annotation { "Feature Type Name" : "Feature", "Feature Type Description" : "" }
export const myFeature = defineFeature(function(context is Context, id is Id, definition is map)
    precondition{}
    {
        {
            var Q0;
            Q0=qCreatedBy(makeId("Front.planeOp"),FACE);
            var sketch = newSketch(context, id + "F0", { "sketchPlane" : qUnion([Q0])});
            skLineSegment(sketch, "E0.bottom", {"start": v(-148.5, 105) * mm, "end": v(148.5, 105) * mm});
            skLineSegment(sketch, "E0.top", {"start": v(-148.5, -105) * mm, "end": v(148.5, -105) * mm});
            skLineSegment(sketch, "E0.left", {"start": v(-148.5, 105) * mm, "end": v(-148.5, -105) * mm});
            skLineSegment(sketch, "E0.right", {"start": v(148.5, 105) * mm, "end": v(148.5, -105) * mm});
            skPoint(sketch, "E0.middle", {"position": v(0, 0) * mm});
            skLineSegment(sketch, "E1", {"start": v(-148.5, 75) * mm, "end": v(101.5, 75) * mm});
            skLineSegment(sketch, "E2", {"start": v(101.5, 105) * mm, "end": v(101.5, 75) * mm});
            skLineSegment(sketch, "E3", {"start": v(-148.5, 45) * mm, "end": v(51.5, 45) * mm});
            skLineSegment(sketch, "E4", {"start": v(101.5, 45) * mm, "end": v(101.5, 75) * mm});
            skCircle(sketch, "E5", {"center": v(-133.5, 90) * mm, "radius": 1.5 * mm});
            skCircle(sketch, "E6", {"center": v(-88.5, 90) * mm, "radius": 1.5 * mm});
            skText(sketch, "E7", { "text": "UPPER ARM - INSIDE - LEFT\n    <<< BACK -- FRONT >>>", "fontName": "Arimo-Regular.ttf"});
            skCircle(sketch, "E8.MirrorC", {"center": v(-133.5, 60) * mm, "radius": 1.5 * mm});
            skCircle(sketch, "E9.MirrorC", {"center": v(-88.5, 60) * mm, "radius": 1.5 * mm});
            skText(sketch, "E10", { "text": "UPPER ARM - INSIDE - RIGHT\n   <<< FRONT -- BACK >>>", "fontName": "OpenSans-Regular.ttf"});
            skLineSegment(sketch, "E11.bottom", {"start": v(73, 85) * mm, "end": v(79, 85) * mm});
            skLineSegment(sketch, "E11.top", {"start": v(73, 95) * mm, "end": v(79, 95) * mm});
            skLineSegment(sketch, "E11.left", {"start": v(73, 85) * mm, "end": v(73, 95) * mm});
            skLineSegment(sketch, "E11.right", {"start": v(79, 85) * mm, "end": v(79, 95) * mm});
            skPoint(sketch, "E11.middle", {"position": v(76, 90) * mm});
            skLineSegment(sketch, "E12", {"start": v(-148.5, 15) * mm, "end": v(51.5, 15) * mm});
            skLineSegment(sketch, "E13", {"start": v(51.5, 15) * mm, "end": v(51.5, 45) * mm});
            skLineSegment(sketch, "E14", {"start": v(-148.5, -15) * mm, "end": v(51.5, -15) * mm});
            skLineSegment(sketch, "E15", {"start": v(51.5, -15) * mm, "end": v(51.5, 15) * mm});
            skCircle(sketch, "E16", {"center": v(36.5, 30) * mm, "radius": 1.5 * mm});
            skPoint(sketch, "E16.centerSnap0", {"position": v(51.5, 30) * mm});
            skCircle(sketch, "E17", {"center": v(-53.5, 35) * mm, "radius": 1.5 * mm});
            skCircle(sketch, "E18", {"center": v(-78.5, 25) * mm, "radius": 1.5 * mm});
            skCircle(sketch, "E19", {"center": v(-133.5, 30) * mm, "radius": 1.5 * mm});
            skText(sketch, "E20", { "text": "MIDDLE ARM - INSIDE - LEFT\n   <<< BOTTOM -- TOP >>>", "fontName": "OpenSans-Regular.ttf"});
            skLineSegment(sketch, "E21", {"start": v(-108.5, 45) * mm, "end": v(-108.5, 39) * mm});
            skLineSegment(sketch, "E22", {"start": v(-108.5, 39) * mm, "end": v(-98.5, 39) * mm});
            skLineSegment(sketch, "E23", {"start": v(-98.5, 39) * mm, "end": v(-98.5, 45) * mm});
            skCircle(sketch, "E24.MirrorC", {"center": v(-133.5, 0) * mm, "radius": 1.5 * mm});
            skCircle(sketch, "E25.MirrorC", {"center": v(-53.5, -5) * mm, "radius": 1.5 * mm});
            skCircle(sketch, "E26.MirrorC", {"center": v(-78.5, 5) * mm, "radius": 1.5 * mm});
            skCircle(sketch, "E27.MirrorC", {"center": v(36.5, 0) * mm, "radius": 1.5 * mm});
            skLineSegment(sketch, "E28.MirrorCS", {"start": v(-108.5, -9) * mm, "end": v(-98.5, -9) * mm});
            skLineSegment(sketch, "E29.MirrorCS", {"start": v(-98.5, -9) * mm, "end": v(-98.5, -15) * mm});
            skLineSegment(sketch, "E30.MirrorCS", {"start": v(-108.5, -15) * mm, "end": v(-108.5, -9) * mm});
            skText(sketch, "E31", { "text": "MIDDLE ARM - INSIDE - RIGHT\n   <<< TOP -- BOTTOM >>>", "fontName": "OpenSans-Regular.ttf"});
            skLineSegment(sketch, "E32", {"start": v(51.5, -15) * mm, "end": v(51.5, -85) * mm});
            skLineSegment(sketch, "E33", {"start": v(81.5, 45) * mm, "end": v(118.5, -85.1) * mm});
            skLineSegment(sketch, "E34", {"start": v(51.5, 45) * mm, "end": v(81.5, 45) * mm});
            skLineSegment(sketch, "E35", {"start": v(81.5, 45) * mm, "end": v(101.5, 45) * mm});
            skCircle(sketch, "E36", {"center": v(66.5, 30) * mm, "radius": 1.5 * mm});
            skPoint(sketch, "E36.centerSnap0", {"position": v(66.5, 45) * mm});
            skLineSegment(sketch, "E37", {"start": v(148.5, -85.1) * mm, "end": v(118.5, -85.1) * mm});
            skCircle(sketch, "E38", {"center": v(95.2, -39.74) * mm, "radius": 1.5 * mm});
            skCircle(sketch, "E39", {"center": v(104.8, -0.36) * mm, "radius": 1.5 * mm});
            skCircle(sketch, "E40", {"center": v(133.5, -70.1) * mm, "radius": 1.5 * mm});
            skPoint(sketch, "E40.centerSnap0", {"position": v(133.5, -85.1) * mm});
            skPoint(sketch, "E41.endSnap0", {"position": v(91.5, 45) * mm});
            skLineSegment(sketch, "E42", {"start": v(95.2, -39.74) * mm, "end": v(104.82, -37) * mm, "construction": true});
            skLineSegment(sketch, "E43", {"start": v(104.8, -0.36) * mm, "end": v(95.18, -3.1) * mm, "construction": true});
            skLineSegment(sketch, "E44", {"start": v(51.5, -85) * mm, "end": v(-18.5, -85) * mm});
            skLineSegment(sketch, "E45", {"start": v(-18.5, -85) * mm, "end": v(-18.5, -15) * mm});
            skLineSegment(sketch, "E46", {"start": v(-24.5, -15) * mm, "end": v(-24.5, -25) * mm});
            skLineSegment(sketch, "E47", {"start": v(-24.5, -25) * mm, "end": v(-18.5, -25) * mm});
            skLineSegment(sketch, "E48", {"start": v(-18.5, -35) * mm, "end": v(-24.5, -35) * mm});
            skLineSegment(sketch, "E49", {"start": v(-24.5, -35) * mm, "end": v(-24.5, -45) * mm});
            skLineSegment(sketch, "E50", {"start": v(-24.5, -45) * mm, "end": v(-49.5, -45) * mm});
            skLineSegment(sketch, "E51", {"start": v(-49.5, -45) * mm, "end": v(-49.5, -35) * mm});
            skLineSegment(sketch, "E52", {"start": v(-49.5, -35) * mm, "end": v(-55.5, -35) * mm});
            skLineSegment(sketch, "E53", {"start": v(-55.5, -35) * mm, "end": v(-55.5, -25) * mm});
            skLineSegment(sketch, "E54", {"start": v(-55.5, -25) * mm, "end": v(-49.5, -25) * mm});
            skLineSegment(sketch, "E55", {"start": v(-49.5, -25) * mm, "end": v(-49.5, -15) * mm});
            skLineSegment(sketch, "E56.MirrorCS", {"start": v(-86.5, -15) * mm, "end": v(-86.5, -25) * mm});
            skLineSegment(sketch, "E57.MirrorCS", {"start": v(-61.5, -45) * mm, "end": v(-61.5, -35) * mm});
            skLineSegment(sketch, "E58.MirrorCS", {"start": v(-86.5, -35) * mm, "end": v(-86.5, -45) * mm});
            skLineSegment(sketch, "E59.MirrorCS", {"start": v(-55.5, -25) * mm, "end": v(-61.5, -25) * mm});
            skLineSegment(sketch, "E60.MirrorCS", {"start": v(-86.5, -25) * mm, "end": v(-92.5, -25) * mm});
            skLineSegment(sketch, "E61.MirrorCS", {"start": v(-61.5, -35) * mm, "end": v(-55.5, -35) * mm});
            skLineSegment(sketch, "E62.MirrorCS", {"start": v(-61.5, -25) * mm, "end": v(-61.5, -15) * mm});
            skLineSegment(sketch, "E63.MirrorCS", {"start": v(-86.5, -45) * mm, "end": v(-61.5, -45) * mm});
            skLineSegment(sketch, "E64.MirrorCS", {"start": v(-92.5, -35) * mm, "end": v(-86.5, -35) * mm});
            skLineSegment(sketch, "E65", {"start": v(-92.5, -25) * mm, "end": v(-92.5, -35) * mm});
            skLineSegment(sketch, "E66.MirrorCS", {"start": v(-92.5, -35) * mm, "end": v(-98.5, -35) * mm});
            skLineSegment(sketch, "E67.MirrorCS", {"start": v(-98.5, -25) * mm, "end": v(-92.5, -25) * mm});
            skLineSegment(sketch, "E68.MirrorCS", {"start": v(-98.5, -35) * mm, "end": v(-98.5, -45) * mm});
            skLineSegment(sketch, "E69.MirrorCS", {"start": v(-98.5, -15) * mm, "end": v(-98.5, -25) * mm});
            skLineSegment(sketch, "E70", {"start": v(-98.5, -45) * mm, "end": v(-138.5, -45) * mm});
            skLineSegment(sketch, "E71", {"start": v(-118.5, -45) * mm, "end": v(-118.5, -15) * mm, "construction": true});
            skLineSegment(sketch, "E72.MirrorCS", {"start": v(-138.5, -35) * mm, "end": v(-138.5, -45) * mm});
            skLineSegment(sketch, "E73.MirrorCS", {"start": v(-144.5, -35) * mm, "end": v(-138.5, -35) * mm});
            skLineSegment(sketch, "E74.MirrorCS", {"start": v(-138.5, -15) * mm, "end": v(-138.5, -25) * mm});
            skLineSegment(sketch, "E75.MirrorCS", {"start": v(-144.5, -25) * mm, "end": v(-144.5, -35) * mm});
            skLineSegment(sketch, "E76.MirrorCS", {"start": v(-138.5, -25) * mm, "end": v(-144.5, -25) * mm});
            skText(sketch, "E77", { "text": "      SPACER\nMIDDLE - ARM", "fontName": "OpenSans-Regular.ttf"});
            skText(sketch, "E78", { "text": "   SPACER\nTOP - ARM\n   FRONT", "fontName": "OpenSans-Regular.ttf"});
            skPoint(sketch, "E79", {"position": v(-74, -45) * mm});
            skPoint(sketch, "E80", {"position": v(-37, -45) * mm});
            skText(sketch, "E81", { "text": "   SPACER\nTOP - ARM", "fontName": "OpenSans-Regular.ttf"});
            skLineSegment(sketch, "E82", {"start": v(-18.5, -51) * mm, "end": v(-28.5, -51) * mm});
            skLineSegment(sketch, "E83", {"start": v(-28.5, -51) * mm, "end": v(-28.5, -45) * mm});
            skLineSegment(sketch, "E84", {"start": v(-43.5, -45) * mm, "end": v(-43.5, -51) * mm});
            skLineSegment(sketch, "E85", {"start": v(-43.5, -51) * mm, "end": v(-83.5, -51) * mm});
            skLineSegment(sketch, "E86", {"start": v(-83.5, -51) * mm, "end": v(-83.5, -63.5) * mm, "construction": true});
            skLineSegment(sketch, "E87", {"start": v(-18.5, -63.5) * mm, "end": v(-148.5, -63.5) * mm, "construction": true});
            skLineSegment(sketch, "E88.MirrorCS", {"start": v(-43.5, -76) * mm, "end": v(-83.5, -76) * mm});
            skLineSegment(sketch, "E89.MirrorCS", {"start": v(-28.5, -76) * mm, "end": v(-28.5, -82) * mm});
            skLineSegment(sketch, "E90.MirrorCS", {"start": v(-43.5, -82) * mm, "end": v(-43.5, -76) * mm});
            skLineSegment(sketch, "E91.MirrorCS", {"start": v(-18.5, -76) * mm, "end": v(-28.5, -76) * mm});
            skLineSegment(sketch, "E92", {"start": v(-43.5, -82) * mm, "end": v(-28.5, -82) * mm});
            skLineSegment(sketch, "E93", {"start": v(-18.5, -85) * mm, "end": v(-18.5, -76) * mm});
            skLineSegment(sketch, "E94.MirrorCS", {"start": v(-148.5, -85) * mm, "end": v(-148.5, -76) * mm});
            skLineSegment(sketch, "E95.MirrorCS", {"start": v(-148.5, -76) * mm, "end": v(-138.5, -76) * mm});
            skLineSegment(sketch, "E96.MirrorCS", {"start": v(-138.5, -76) * mm, "end": v(-138.5, -82) * mm});
            skLineSegment(sketch, "E97.MirrorCS", {"start": v(-123.5, -45) * mm, "end": v(-123.5, -51) * mm});
            skLineSegment(sketch, "E98.MirrorCS", {"start": v(-123.5, -82) * mm, "end": v(-138.5, -82) * mm});
            skLineSegment(sketch, "E99.MirrorCS", {"start": v(-148.5, -51) * mm, "end": v(-138.5, -51) * mm});
            skLineSegment(sketch, "E100.MirrorCS", {"start": v(-123.5, -51) * mm, "end": v(-83.5, -51) * mm});
            skLineSegment(sketch, "E101.MirrorCS", {"start": v(-123.5, -82) * mm, "end": v(-123.5, -76) * mm});
            skLineSegment(sketch, "E102.MirrorCS", {"start": v(-123.5, -76) * mm, "end": v(-83.5, -76) * mm});
            skLineSegment(sketch, "E103.MirrorCS", {"start": v(-138.5, -51) * mm, "end": v(-138.5, -45) * mm});
            skLineSegment(sketch, "E104", {"start": v(-148.5, -51) * mm, "end": v(-148.5, -85) * mm});
            skLineSegment(sketch, "E105", {"start": v(-123.5, -45) * mm, "end": v(-61.5, -45) * mm});
            skCircle(sketch, "E106", {"center": v(-28.5, -60) * mm, "radius": 1.5 * mm});
            skCircle(sketch, "E107.MirrorC", {"center": v(-28.5, -67) * mm, "radius": 1.5 * mm});
            skCircle(sketch, "E108.MirrorC", {"center": v(-138.5, -60) * mm, "radius": 1.5 * mm});
            skCircle(sketch, "E109.MirrorC", {"center": v(-138.5, -67) * mm, "radius": 1.5 * mm});
            skLineSegment(sketch, "E110", {"start": v(51.5, 35) * mm, "end": v(57.5, 35) * mm});
            skLineSegment(sketch, "E111", {"start": v(57.5, 35) * mm, "end": v(57.5, 20) * mm});
            skLineSegment(sketch, "E112", {"start": v(57.5, 20) * mm, "end": v(51.5, 20) * mm});
            skLineSegment(sketch, "E113", {"start": v(51.5, -60) * mm, "end": v(57.5, -60) * mm});
            skLineSegment(sketch, "E114", {"start": v(57.5, -60) * mm, "end": v(57.5, -75) * mm});
            skLineSegment(sketch, "E115", {"start": v(57.5, -75) * mm, "end": v(51.5, -75) * mm});
            skLineSegment(sketch, "E116", {"start": v(148.5, -75.1) * mm, "end": v(142.5, -75.1) * mm});
            skLineSegment(sketch, "E117", {"start": v(142.5, -75.1) * mm, "end": v(142.5, -60.1) * mm});
            skLineSegment(sketch, "E118", {"start": v(142.5, -60.1) * mm, "end": v(148.5, -60.1) * mm});
            skLineSegment(sketch, "E119", {"start": v(148.5, 19.9) * mm, "end": v(142.5, 19.9) * mm});
            skLineSegment(sketch, "E120", {"start": v(142.5, 19.9) * mm, "end": v(142.5, 34.9) * mm});
            skLineSegment(sketch, "E121", {"start": v(142.5, 34.9) * mm, "end": v(148.5, 34.9) * mm});
            skLineSegment(sketch, "E122.bottom", {"start": v(20.17, -31.5) * mm, "end": v(35.83, -31.5) * mm});
            skLineSegment(sketch, "E122.top", {"start": v(20.17, -37.5) * mm, "end": v(35.83, -37.5) * mm});
            skLineSegment(sketch, "E122.left", {"start": v(20.17, -31.5) * mm, "end": v(20.17, -37.5) * mm});
            skLineSegment(sketch, "E122.right", {"start": v(35.83, -31.5) * mm, "end": v(35.83, -37.5) * mm});
            skLineSegment(sketch, "E123", {"start": v(35.83, -31.5) * mm, "end": v(51.5, -31.5) * mm, "construction": true});
            skLineSegment(sketch, "E124", {"start": v(51.5, -50) * mm, "end": v(17.52, -50) * mm, "construction": true});
            skPoint(sketch, "E124.endSnap0", {"position": v(51.5, -50) * mm});
            skLineSegment(sketch, "E125.MirrorCS", {"start": v(20.17, -62.5) * mm, "end": v(35.83, -62.5) * mm});
            skLineSegment(sketch, "E126.MirrorCS", {"start": v(20.17, -68.5) * mm, "end": v(20.17, -62.5) * mm});
            skLineSegment(sketch, "E127.MirrorCS", {"start": v(20.17, -68.5) * mm, "end": v(35.83, -68.5) * mm});
            skLineSegment(sketch, "E128.MirrorCS", {"start": v(35.83, -68.5) * mm, "end": v(35.83, -62.5) * mm});
            skText(sketch, "E129", { "text": "SPACER BASE", "fontName": "OpenSans-Regular.ttf"});
            skText(sketch, "E130", { "text": "BASE", "fontName": "OpenSans-Regular.ttf"});
            skText(sketch, "E131", { "text": "BASE\nSIDE WALL\nRIGHT", "fontName": "OpenSans-Regular.ttf"});
            skText(sketch, "E132", { "text": "BASE\nSIDE WALL\nLEFT", "fontName": "OpenSans-Regular.ttf"});
            skLineSegment(sketch, "E133", {"start": v(101.5, 45) * mm, "end": v(117.17, 45) * mm});
            skLineSegment(sketch, "E134", {"start": v(117.17, 45) * mm, "end": v(117.17, 51) * mm});
            skLineSegment(sketch, "E135", {"start": v(117.17, 51) * mm, "end": v(132.83, 51) * mm});
            skLineSegment(sketch, "E136", {"start": v(132.83, 51) * mm, "end": v(132.83, 45) * mm});
            skLineSegment(sketch, "E137", {"start": v(132.83, 45) * mm, "end": v(148.5, 45) * mm});
            skLineSegment(sketch, "E138", {"start": v(51.5, -85) * mm, "end": v(67.17, -85) * mm});
            skLineSegment(sketch, "E139", {"start": v(67.17, -85) * mm, "end": v(67.17, -91) * mm});
            skLineSegment(sketch, "E140", {"start": v(67.17, -91) * mm, "end": v(82.83, -91) * mm});
            skLineSegment(sketch, "E141", {"start": v(82.83, -91) * mm, "end": v(82.83, -85) * mm});
            skLineSegment(sketch, "E142", {"start": v(82.83, -85) * mm, "end": v(118.5, -85.1) * mm});
            skText(sketch, "E143", { "text": "HYDRAULIC CARDBOARD ROBOT\nA4 TEMPLATE OF ARM PARTS\nPRINT ON A4 PAPER, GLUE TO 6MM CARDBOARD, CUT ALL LINES, DRILL HOLES WITH 2MM DRILL", "fontName": "OpenSans-Regular.ttf"});
            skLineSegment(sketch, "E144", {"start": v(91.5, 105) * mm, "end": v(91.5, 99) * mm});
            skLineSegment(sketch, "E145", {"start": v(91.5, 99) * mm, "end": v(79, 99) * mm});
            skLineSegment(sketch, "E146", {"start": v(79, 99) * mm, "end": v(79, 105) * mm});
            skLineSegment(sketch, "E147.MirrorCS", {"start": v(91.5, 45) * mm, "end": v(91.5, 51) * mm});
            skLineSegment(sketch, "E148.MirrorCS", {"start": v(79, 51) * mm, "end": v(79, 45) * mm});
            skLineSegment(sketch, "E149.MirrorCS", {"start": v(91.5, 51) * mm, "end": v(79, 51) * mm});
            skLineSegment(sketch, "E150", {"start": v(-70, -15) * mm, "end": v(-70, -21) * mm});
            skLineSegment(sketch, "E151", {"start": v(-70, -21) * mm, "end": v(-78, -21) * mm});
            skLineSegment(sketch, "E152", {"start": v(-78, -21) * mm, "end": v(-78, -15) * mm});
            skPoint(sketch, "E153", {"position": v(-74, -21) * mm});
            skPoint(sketch, "E154", {"position": v(101.5, 90) * mm});
            skLineSegment(sketch, "E155.MirrorCS", {"start": v(73, 55) * mm, "end": v(79, 55) * mm});
            skPoint(sketch, "E156.MirrorP", {"position": v(76, 60) * mm});
            skLineSegment(sketch, "E157.MirrorCS", {"start": v(79, 65) * mm, "end": v(79, 55) * mm});
            skLineSegment(sketch, "E158.MirrorCS", {"start": v(73, 65) * mm, "end": v(79, 65) * mm});
            skLineSegment(sketch, "E159.MirrorCS", {"start": v(73, 65) * mm, "end": v(73, 55) * mm});
            skLineSegment(sketch, "E160.bottom", {"start": v(-62.5, 95) * mm, "end": v(-68.5, 95) * mm});
            skLineSegment(sketch, "E160.top", {"start": v(-62.5, 85) * mm, "end": v(-68.5, 85) * mm});
            skLineSegment(sketch, "E160.left", {"start": v(-62.5, 95) * mm, "end": v(-62.5, 85) * mm});
            skLineSegment(sketch, "E160.right", {"start": v(-68.5, 95) * mm, "end": v(-68.5, 85) * mm});
            skPoint(sketch, "E160.middle", {"position": v(-65.5, 90) * mm});
            skPoint(sketch, "E161.MirrorP", {"position": v(-65.5, 60) * mm});
            skLineSegment(sketch, "E162.MirrorCS", {"start": v(-68.5, 55) * mm, "end": v(-68.5, 65) * mm});
            skLineSegment(sketch, "E163.MirrorCS", {"start": v(-62.5, 65) * mm, "end": v(-68.5, 65) * mm});
            skLineSegment(sketch, "E164.MirrorCS", {"start": v(-62.5, 55) * mm, "end": v(-62.5, 65) * mm});
            skLineSegment(sketch, "E165.MirrorCS", {"start": v(-62.5, 55) * mm, "end": v(-68.5, 55) * mm});
            skLineSegment(sketch, "E166.bottom", {"start": v(67.93, -52.8) * mm, "end": v(88.5, -52.8) * mm});
            skLineSegment(sketch, "E166.top", {"start": v(67.93, -46.04) * mm, "end": v(88.5, -46.04) * mm});
            skLineSegment(sketch, "E166.left", {"start": v(67.93, -52.8) * mm, "end": v(67.93, -46.04) * mm});
            skLineSegment(sketch, "E166.right", {"start": v(88.5, -52.8) * mm, "end": v(88.5, -46.04) * mm});
            skText(sketch, "E167", { "text": "RIGHT", "fontName": "OpenSans-Regular.ttf"});
            const initialGuessF0  = {"E7": [-0.05021, 0.09, 1, 0, 0.0025], "E10": [-0.00357, 0.06, -1, 0, 0.0025], "E20": [-0.12632, 0.03, 1, 0, 0.0025], "E31": [-0.0793, 0, -1, 0, 0.0025], "E77": [-0.12585, -0.03158, 1, 0, 0.00158], "E78": [-0.07939, -0.03158, 1, 0, 0.00158], "E81": [-0.04239, -0.03158, 1, 0, 0.00158], "E129": [-0.0852, -0.05775, 1, 0, 0.00147], "E130": [-0.01112, -0.05666, 1, 0, 0.00275], "E131": [0.06108, -0.06356, 1, 0, 0.00298], "E132": [0.13541, 0.02407, -0.99985, -0.0172, 0.00298], "E143": [-0.01016, -0.09257, 1, 0, 0.00244], "E167": [-0.00456, -0.02022, 1, 0, 0.00117]};
            skSetInitialGuess(sketch, initialGuessF0);
            skSolve(sketch);
        }
        {
            var Q0;
            Q0=makeQuery(id+"F0.imprint","IMPRINT",FACE,{"disambiguationData":[TD([[makeQuery(id+"F0.imprint","IMPRINT",EDGE,{"derivedFrom":sQuery(id+"F0.wireOp",EDGE,"E65")}),-1.0]])]});
            var Q1;
            {var subQ0=sQuery(id+"F0.wireOp",EDGE,"E46");Q1=makeQuery(id+"F0.imprint","IMPRINT",FACE,{"disambiguationData":[TD([[makeQuery(id+"F0.imprint","IMPRINT",EDGE,{"derivedFrom":subQ0}),-1.0]])]});}
            var Q2;
            {var subQ3=sQuery(id+"F0.wireOp",EDGE,"E1");Q2=makeQuery(id+"F0.imprint","IMPRINT",FACE,{"disambiguationData":[TD([[makeQuery(id+"F0.imprint","IMPRINT",EDGE,{"derivedFrom":subQ3}),1.0]])]});}
            var Q3;
            {var subQ6=sQuery(id+"F0.wireOp",EDGE,"E12");Q3=makeQuery(id+"F0.imprint","IMPRINT",FACE,{"disambiguationData":[TD([[makeQuery(id+"F0.imprint","IMPRINT",EDGE,{"derivedFrom":subQ6}),1.0]])]});}
            var Q4;
            {var subQ3=sQuery(id+"F0.wireOp",EDGE,"E33");Q4=makeQuery(id+"F0.imprint","IMPRINT",FACE,{"disambiguationData":[TD([[makeQuery(id+"F0.imprint","IMPRINT",EDGE,{"derivedFrom":subQ3}),1.0]])]});}
            extrude(context, id + "F1", {"entities" : qUnion([Q0, Q1, Q2, Q3, Q4]), "depth" : 6 * mm, "offsetDistance" : 25 * mm});
        }
        {
            var Q0;
            {var subQ8=sQuery(id+"F0.wireOp",EDGE,"E1");Q0=makeQuery(id+"F0.imprint","IMPRINT",FACE,{"disambiguationData":[TD([[makeQuery(id+"F0.imprint","IMPRINT",EDGE,{"derivedFrom":subQ8}),-1.0]])]});}
            var Q1;
            {var subQ8=sQuery(id+"F0.wireOp",EDGE,"E12");Q1=makeQuery(id+"F0.imprint","IMPRINT",FACE,{"disambiguationData":[TD([[makeQuery(id+"F0.imprint","IMPRINT",EDGE,{"derivedFrom":subQ8}),-1.0]])]});}
            extrude(context, id + "F2", {"entities" : qUnion([Q0, Q1]), "depth" : 6 * mm, "offsetDistance" : 25 * mm});
        }
        {
            var Q0;
            {var subQ4=sQuery(id+"F0.wireOp",EDGE,"E15");Q0=makeQuery(id+"F0.imprint","IMPRINT",FACE,{"disambiguationData":[TD([[makeQuery(id+"F0.imprint","IMPRINT",EDGE,{"derivedFrom":subQ4}),-1.0]])]});}
            var Q1;
            Q1=makeQuery(id+"F0.imprint","IMPRINT",FACE,{"disambiguationData":[TD([[makeQuery(id+"F0.imprint","IMPRINT",EDGE,{"derivedFrom":sQuery(id+"F0.wireOp",EDGE,"E53")}),1.0]])]});
            extrude(context, id + "F3", {"entities" : qUnion([Q0, Q1]), "depth" : 6 * mm, "offsetDistance" : 25 * mm});
        }
        {
            var Q0;
            {var subQ11=sQuery(id+"F0.wireOp",EDGE,"E44");Q0=makeQuery(id+"F0.imprint","IMPRINT",FACE,{"disambiguationData":[TD([[makeQuery(id+"F0.imprint","IMPRINT",EDGE,{"derivedFrom":subQ11}),-1.0]])]});}
            extrude(context, id + "F4", {"entities" : qUnion([Q0]), "depth" : 6 * mm, "offsetDistance" : 25 * mm});
        }
        {
            var Q0;
            Q0=makeQuery(id+"F0.imprint","IMPRINT",FACE,{"disambiguationData":[TD([[makeQuery(id+"F0.imprint","IMPRINT",EDGE,{"derivedFrom":sQuery(id+"F0.wireOp",EDGE,"E70")}),1.0]])]});
            extrude(context, id + "F5", {"entities" : qUnion([Q0]), "depth" : 6 * mm, "offsetDistance" : 25 * mm});
        }
    });